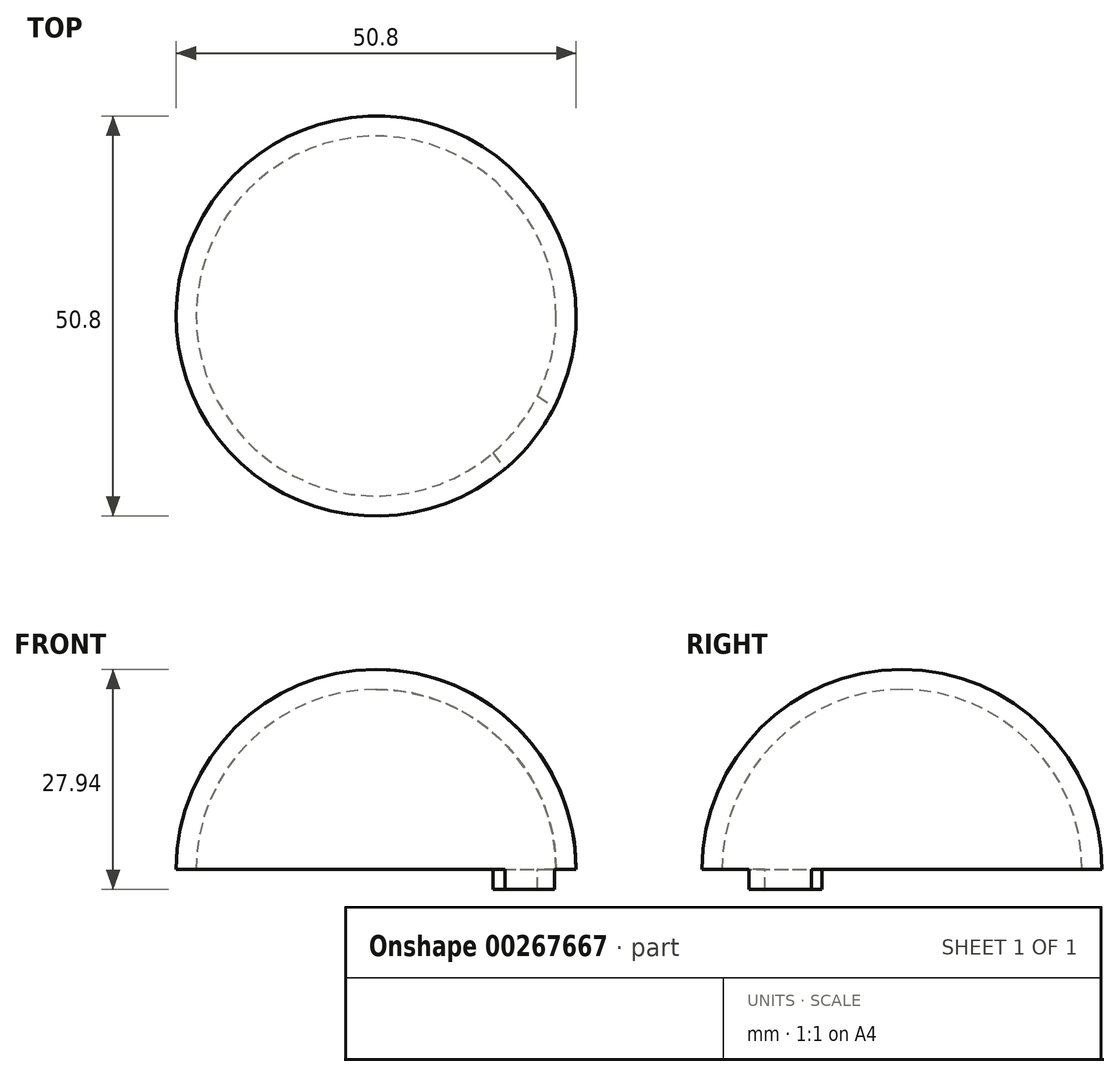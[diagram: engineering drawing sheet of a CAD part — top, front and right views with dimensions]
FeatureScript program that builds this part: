
annotation { "Feature Type Name" : "Feature", "Feature Type Description" : "" }
export const myFeature = defineFeature(function(context is Context, id is Id, definition is map)
    precondition{}
    {
        {
            var Q0;
            Q0=qCreatedBy(makeId("Front.planeOp"),FACE);
            var sketch = newSketch(context, id + "F0", { "sketchPlane" : qUnion([Q0])});
            skArc(sketch, "E0", {"start": v(25.4, 0) * mm, "mid": v(17.96, 17.96) * mm, "end": v(0, 25.4) * mm});
            skArc(sketch, "E1.0", {"start": v(22.86, 0) * mm, "mid": v(16.16, 16.16) * mm, "end": v(0, 22.86) * mm});
            skLineSegment(sketch, "E2", {"start": v(0, 22.86) * mm, "end": v(0, 25.4) * mm});
            skLineSegment(sketch, "E3", {"start": v(25.4, 0) * mm, "end": v(22.86, 0) * mm});
            skSolve(sketch);
        }
        {
            var Q0;
            Q0=makeQuery(id+"F0.imprint","IMPRINT",FACE,{"disambiguationData":[TD([[makeQuery(id+"F0.imprint","IMPRINT",EDGE,{"derivedFrom":sQuery(id+"F0.wireOp",EDGE,"E0")}),1.0]])]});
            var Q1;
            Q1=sQuery(id+"F0.wireOp",EDGE,"E2");
            revolve(context, id + "F1", {"entities" : qUnion([Q0]), "axis" : qUnion([Q1]), "revolveType" : RevolveType.FULL});
        }
        {
            var Q0;
            Q0=makeQuery(id+"F1.opRevolve","SWEPT_FACE",FACE,{"disambiguationData":[OSD([sQuery(id+"F0.wireOp",EDGE,"E3")])]});
            var sketch = newSketch(context, id + "F2", { "sketchPlane" : qUnion([Q0])});
            skLineSegment(sketch, "E4", {"start": v(14.81, 17.41) * mm, "end": v(16.35, 19.44) * mm});
            skLineSegment(sketch, "E5", {"start": v(20.47, 10.17) * mm, "end": v(22.63, 11.54) * mm});
            skSolve(sketch);
        }
        {
            var Q0;
            {var subQ0=sQuery(id+"F2.wireOp",EDGE,"E4");Q0=makeQuery(id+"F2.imprint","IMPRINT",FACE,{"disambiguationData":[TD([[makeQuery(id+"F2.imprint","IMPRINT",EDGE,{"derivedFrom":subQ0}),-1.0]])]});}
            extrude(context, id + "F3", {"entities" : qUnion([Q0]), "operationType" : NewBodyOperationType.ADD, "depth" : 2.54 * mm});
        }
    });
